# Revit family: TY-FRB-TY313_Metric
name_source: partatom
category: Sprinklers
revit_build: Autodesk Revit 2016 (Build: 20150220_1215(x64)
units: mm (PartAtom-declared; Revit-internal decimal feet)

## family parameters
Always vertical = Yes
Cut with Voids When Loaded = No
Maintain Annotation Orientation = No
OmniClass Number = 23.65.70.17.11.24
OmniClass Title = Fire Fighting Sprinkler Heads
Part Type = Normal
Room Calculation Point = No
Round Connector Dimension = Use Diameter
Shared = No
Work Plane-Based = No

## types (22) — shared parameters
COBie = Yes
COBie.Type = Yes
COBie.Type.AssetType = Fixed
COBie.Type.Category = Pr_70_55_97_84:Sprinklers
COBie.Type.DurationUnit = year
COBie.Type.Manufacturer = Tyco Fire Protection Products
COBie.Type.Material = Bronze
COBie.Type.Size = 1/2"(DN15)
COBie.Type.WarrantyGuarantorParts = http://tycofsbp.com
Coverage = Standard
Coverage_ = Standard
K-Factor = 79.9096
Manufacturer = Tyco Fire Protection Products
Manufacturer URL = www.tyco-fire.com
Material_ = Bronze
Model = TY-FRB
Nominal Diameter 1 = 15 mm
Orifice = Standard
Orifice Size = 11 mm
Outside Diameter 1 = 21 mm
Response = Quick
Response_ = Quick
SIN No = TY313
Takeout 1 = 51 mm
Technical Data Sheet No = TFP172
zero-valued in all types: COBie.Type.NominalHeight, COBie.Type.NominalLength, COBie.Type.NominalWidth, COBie.Type.ReplacementCost, Style Id

## per-type parameters (varying)
| type | COBie.Component.Description | COBie.Component.Name | COBie.Type.Colour | COBie.Type.Finish | COBie.Type.ModelNumber | COBie.Type.ModelReference | COBie.Type.Shape | Description | Finish_ | Part No | Temperature Rating |
| Wet Upright_135  57.2°C K80 DN15 NPT Br_77-370-1-135 | TY-FRB Wet Upright_135  57.2°C K80 DN15 NPT Br | Sprinklers:Upright_135 | Yellow | Natural Brass | 77-370-1-135 | TY-FRB Wet Upright_135  57.2°C K80 DN15 NPT Br | Cylinder | TY-FRB Wet Upright_135  57.2°C K80 DN15 NPT Br | Natural Brass | 77-370-1-135 | 57 °C |
| Wet Upright_155  68.3°C K80 DN15 NPT Br_77-370-1-155 | TY-FRB Wet Upright_155  68.3°C K80 DN15 NPT Br | Sprinklers:Upright_155 | Yellow | Natural Brass | 77-370-1-155 | TY-FRB Wet Upright_155  68.3°C K80 DN15 NPT Br | Cylinder | TY-FRB Wet Upright_155  68.3°C K80 DN15 NPT Br | Natural Brass | 77-370-1-155 | 68 °C |
| Wet Upright_175  79.4°C K80 DN15 NPT Br_77-370-1-175 | TY-FRB Wet Upright_175  79.4°C K80 DN15 NPT Br | Sprinklers:Upright_175 | Yellow | Natural Brass | 77-370-1-175 | TY-FRB Wet Upright_175  79.4°C K80 DN15 NPT Br | Cylinder | TY-FRB Wet Upright_175  79.4°C K80 DN15 NPT Br | Natural Brass | 77-370-1-175 | 79 °C |
| Wet Upright_200  93.3°C K80 DN15 NPT Br_77-370-1-200 | TY-FRB Wet Upright_200  93.3°C K80 DN15 NPT Br | Sprinklers:Upright_200 | Yellow | Natural Brass | 77-370-1-200 | TY-FRB Wet Upright_200  93.3°C K80 DN15 NPT Br | Cylinder | TY-FRB Wet Upright_200  93.3°C K80 DN15 NPT Br | Natural Brass | 77-370-1-200 | 93 °C |
| Wet Upright_286  141.1°C K80 DN15 NPT Br_77-370-1-286 | TY-FRB Wet Upright_286  141.1°C K80 DN15 NPT Br | Sprinklers:Upright_286 | Yellow | Natural Brass | 77-370-1-286 | TY-FRB Wet Upright_286  141.1°C K80 DN15 NPT Br | Cylinder | TY-FRB Wet Upright_286  141.1°C K80 DN15 NPT Br | Natural Brass | 77-370-1-286 | 141 °C |
| Wet Upright_135  57.2°C K80 DN15 NPT Wh9010_77-370-3-135 | TY-FRB Wet Upright_White_135  57.2°C K80 DN15 NPT Wh9010 | Sprinklers:Upright_135 | White | Pure White | 77-370-3-135 | TY-FRB Wet Upright_White_135  57.2°C K80 DN15 NPT Wh9010 | Cylinder | TY-FRB Wet Upright_135  57.2°C K80 DN15 NPT Wh9010 | White RAL9010 | 77-370-3-135 | 57 °C |
| Wet Upright_155  68.3°C K80 DN15 NPT Wh9010_77-370-3-155 | TY-FRB Wet Upright_White_155  68.3°C K80 DN15 NPT Wh9010 | Sprinklers:Upright_155 | White | Pure White | 77-370-3-155 | TY-FRB Wet Upright_White_155  68.3°C K80 DN15 NPT Wh9010 | Cylinder | TY-FRB Wet Upright_155  68.3°C K80 DN15 NPT Wh9010 | White RAL9010 | 77-370-3-155 | 68 °C |
| Wet Upright_175  79.4°C K80 DN15 NPT Wh9010_77-370-3-175 | TY-FRB Wet Upright_175  79.4°C K80 DN15 NPT Wh9010 | Sprinklers:Upright_175 | White | Pure White | 77-370-3-175 | TY-FRB Wet Upright_175  79.4°C K80 DN15 NPT Wh9010 | Cylinder | TY-FRB Wet Upright_175  79.4°C K80 DN15 NPT Wh9010 | White RAL9010 | 77-370-3-175 | 79 °C |
| Wet Upright_200  93.3°C K80 DN15 NPT Wh9010_77-370-3-200 | TY-FRB Wet Upright_200  93.3°C K80 DN15 NPT Wh9010 | Sprinklers:Upright_200 | White | Pure White | 77-370-3-200 | TY-FRB Wet Upright_200  93.3°C K80 DN15 NPT Wh9010 | Cylinder | TY-FRB Wet Upright_200  93.3°C K80 DN15 NPT Wh9010 | White RAL9010 | 77-370-3-200 | 93 °C |
| Wet Upright_286  141.1°C K80 DN15 NPT Wh9010_77-370-3-286 | TY-FRB Wet Upright_286  141.1°C K80 DN15 NPT Wh9010 | Sprinklers:Upright_286 | White | Pure White | 77-370-3-286 | TY-FRB Wet Upright_286  141.1°C K80 DN15 NPT Wh9010 | Cylinder | TY-FRB Wet Upright_286  141.1°C K80 DN15 NPT Wh9010 | White RAL9010 | 77-370-3-286 | 141 °C |
| Wet Upright_135  57.2°C K80 DN15 NPT Wh9003_77-370-4-135 | TY-FRB Wet Upright_135  57.2°C K80 DN15 NPT Wh9003 | Sprinklers:Upright_135 | White | Signal White | 77-370-4-135 | TY-FRB Wet Upright_135  57.2°C K80 DN15 NPT Wh9003 | Cylinder | TY-FRB Wet Upright_135  57.2°C K80 DN15 NPT Wh9003 | White RAL9003 | 77-370-4-135 | 57 °C |
| Wet Upright_155  68.3°C K80 DN15 NPT Wh9003_77-370-4-155 | TY-FRB Wet Upright_155  68.3°C K80 DN15 NPT Wh9003 | Sprinklers:Upright_155 | White | Signal White | 77-370-4-155 | TY-FRB Wet Upright_155  68.3°C K80 DN15 NPT Wh9003 | Cylinder | TY-FRB Wet Upright_155  68.3°C K80 DN15 NPT Wh9003 | White RAL9003 | 77-370-4-155 | 68 °C |
| Wet Upright_175  79.4°C K80 DN15 NPT Wh9003_77-370-4-175 | TY-FRB Wet Upright_175  79.4°C K80 DN15 NPT Wh9003 | Sprinklers:Upright_175 | White | Signal White | 77-370-4-175 | TY-FRB Wet Upright_175  79.4°C K80 DN15 NPT Wh9003 | Cylinder | TY-FRB Wet Upright_175  79.4°C K80 DN15 NPT Wh9003 | White RAL9003 | 77-370-4-175 | 79 °C |
| Wet Upright_200  93.3°C K80 DN15 NPT Wh9003_77-370-4-200 | TY-FRB Wet Upright_200  93.3°C K80 DN15 NPT Wh9003 | Sprinklers:Upright_200 | White | Signal White | 77-370-4-200 | TY-FRB Wet Upright_200  93.3°C K80 DN15 NPT Wh9003 | Cylinder | TY-FRB Wet Upright_200  93.3°C K80 DN15 NPT Wh9003 | White RAL9003 | 77-370-4-200 | 93 °C |
| Wet Upright_286  141.1°C K80 DN15 NPT Wh9003_77-370-4-286 | TY-FRB Wet Upright_286  141.1°C K80 DN15 NPT Wh9003 | Sprinklers:Upright_286 | White | Signal White | 77-370-4-286 | TY-FRB Wet Upright_286  141.1°C K80 DN15 NPT Wh9003 | Cylinder | TY-FRB Wet Upright_286  141.1°C K80 DN15 NPT Wh9003 | White RAL9003 | 77-370-4-286 | 141 °C |
| Wet Upright_155   57.2°C K80 DN15 NPT JBlk_77-370-5-155 | TY-FRB Wet Upright_155  57.2°C K80 DN15 NPT JBlk | Sprinklers:Upright_155 | Black | Jet Black | 77-370-5-155 | TY-FRB Wet Upright_155  57.2°C K80 DN15 NPT JBlk | Cylinder | TY-FRB Wet Upright_155   57.2°C K80 DN15 NPT JBlk | Jet Black RAL9005 | 77-370-5-155 | 57 °C |
| Wet Upright_155   57.2°C K80 DN15 NPT JBlk_77-370-5-200 | TY-FRB Wet Upright_200  57.2°C K80 DN15 NPT JBlk | Sprinklers:Upright_200 | Black | Jet Black | 77-370-5-200 | TY-FRB Wet Upright_200  57.2°C K80 DN15 NPT JBlk | Cylinder | TY-FRB Wet Upright_155   57.2°C K80 DN15 NPT JBlk | Jet Black RAL9005 | 77-370-5-200 | 57 °C |
| Wet Upright_135  57.2°C K80 DN15 NPT Chr_77-370-9-135 | TY-FRB Wet Upright_135  57.2°C K80 DN15 NPT Chr | Sprinklers:Upright_135 | Silver | Chrome Plated | 77-370-9-135 | TY-FRB Wet Upright_135  57.2°C K80 DN15 NPT Chr | Cylinder | TY-FRB Wet Upright_135  57.2°C K80 DN15 NPT Chr | Chrome Plated | 77-370-9-135 | 57 °C |
| Wet Upright_155  68.3°C K80 DN15 NPT Chr_77-370-9-155 | TY-FRB Wet Upright_155  68.3°C K80 DN15 NPT Chr | Sprinklers:Upright_155 | Silver | Chrome Plated | 77-370-9-155 | TY-FRB Wet Upright_155  68.3°C K80 DN15 NPT Chr | Cylinder | TY-FRB Wet Upright_155  68.3°C K80 DN15 NPT Chr | Chrome Plated | 77-370-9-155 | 68 °C |
| Wet Upright_175  79.4°C K80 DN15 NPT Chr_77-370-9-175 | TY-FRB Wet Upright_175  79.4°C K80 DN15 NPT Chr | Sprinklers:Upright_175 | Silver | Chrome Plated | 77-370-9-175 | TY-FRB Wet Upright_175  79.4°C K80 DN15 NPT Chr | Cylinder | TY-FRB Wet Upright_175  79.4°C K80 DN15 NPT Chr | Chrome Plated | 77-370-9-175 | 79 °C |
| Wet Upright_200  93.3°C K80 DN15 NPT Chr_77-370-9-200 | TY-FRB Wet Upright_200  93.3°C K80 DN15 NPT Chr | Sprinklers:Upright_200 | Silver | Chrome Plated | 77-370-9-200 | TY-FRB Wet Upright_200  93.3°C K80 DN15 NPT Chr | cylinder | TY-FRB Wet Upright_200  93.3°C K80 DN15 NPT Chr | Chrome Plated | 77-370-9-200 | 93 °C |
| Wet Upright_286  141.1°C K80 DN15 NPT Chr_77-370-9-286 | TY-FRB Wet Upright_286  141.1°C K80 DN15 NPT Chr | Sprinklers:Upright_286 | Silver | Chrome Plated | 77-370-9-286 | TY-FRB Wet Upright_286  141.1°C K80 DN15 NPT Chr | Cylinder | TY-FRB Wet Upright_286  141.1°C K80 DN15 NPT Chr | Chrome Plated | 77-370-9-286 | 141 °C |

## geometry (parser evidence)
native form markers: Blend x2, Sweep x56
no freeform markers — native parametric forms only
